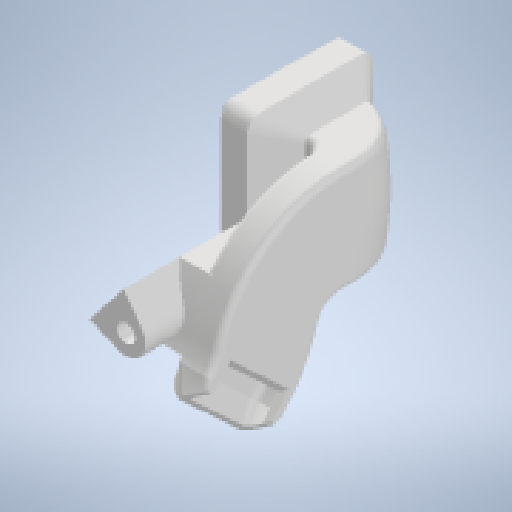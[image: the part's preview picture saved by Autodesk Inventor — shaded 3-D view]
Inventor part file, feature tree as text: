
AUTODESK INVENTOR PART (.ipt)
format: ipt  version: 2023 (Build 270158000, 158)  size: 883,712 bytes
history: native  units: in
note: dims shown in document units (in); Inventor stores cm internally (conversion verified against a paired STEP export)
features: sketch x22, extrude x15, plane x11, reference x9, other x8, loft x6, fillet x3, sweep x2, projected_geometry x2
ambient origin geometry x8: Origin, YZ Plane, XZ Plane, XY Plane, X Axis, Y Axis, Z Axis, Center Point
bodies: Solid1 (feature_tree)
feature tree (78):
  sketch  "Sketch1"  dims[d0=-0.1969in d1=0.7087in d2=0.0in]
  plane  "Work Plane1"
  extrude  "Extrusion1"  Depth=0.7087in TaperAngle=0.0deg
  plane  "Work Plane2"
  sketch  "Sketch3"  dims[d5=0.1575in d6=-0.1575in]
  plane  "Work Plane3"
  extrude  "Extrusion2"  Depth=0.2441in
  extrude  "Extrusion3"  [1 undecoded]
  plane  "Work Plane4"
  sketch  "Sketch5"  dims[d10=0.0984in d11=0.0in d12=-0.0787in]
  extrude  "Extrusion4"  Depth=0.0906in TaperAngle=0.0deg
  extrude  "Extrusion5"  [1 undecoded]
  extrude  "Extrusion6"  Depth=0.4961in
  fillet  "Fillet1"  Radius=0.7776in
  sketch  "Sketch7"  dims[d16=0.6122in d17=0.0394in]
  plane  "Work Plane5"
  sweep  "Sweep1"
  plane  "Work Plane7"
  sketch  "Sketch10"  dims[d20=0.0394in d21=0.0394in]
  loft  "Loft1"
  loft  "Loft2"
  extrude  "Extrusion8"  Depth=0.0689in
  extrude  "Extrusion9"  Depth=0.0689in
  plane  "Work Plane9"
  sketch  "Sketch15"  dims[d26=0.0689in d27=0.9843in]
  extrude  "Extrusion7"  Depth=0.9843in
  loft  "Loft3"
  loft  "Loft4"
  sketch  "Sketch18"  dims[d28=0.315in d29=0.1969in d30=0.0in]
  plane  "Work Plane12"
  sketch  "Sketch23"  dims[d31=0.0787in d32=0.0in d33=0.0787in]
  sketch  "Sketch24"  dims[d34=0.0787in d35=0.0in d36=0.1969in d37=0.0in]
  extrude  "Extrusion11"  Depth=0.1969in TaperAngle=0.0deg
  loft  "Loft6"
  loft  "Loft7"
  sweep  "Sweep2"
  fillet  "Fillet4"  Radius=0.0394in
  sketch  "Sketch30"  dims[d47=0.0in d49=0.125in]
  extrude  "Extrusion12"  Depth=0.0394in
  sketch  "Sketch28"  dims[d42=0.0394in d43=0.0394in d44=0.0394in]
  plane  "Work Plane16"
  extrude  "Extrusion13"  Depth=0.125in
  extrude  "Extrusion14"  Depth=0.5512in
  extrude  "Extrusion15"  TaperAngle=75.0deg  [1 undecoded]
  extrude  "Extrusion16"  Depth=0.1772in
  fillet  "Fillet5"  Radius=0.2756in
  reference  "Reference1"
  sketch  "Sketch2"  dims[d3=0.0906in d4=0.2441in]
  reference  "Reference2"
  reference  "Reference3"
  reference  "Reference4"
  reference  "Reference5"
  reference  "Reference6"
  sketch  "Sketch4"  dims[d7=0.2165in d8=0.0906in d9=0.0in]
  reference  "Reference7"
  sketch  "Sketch6"  dims[d13=0.689in d14=0.4961in d15=0.7776in]
  sketch  "Sketch8"  dims[d18=0.0394in d19=0.0394in]
  plane  "Work Plane6"
  other  "Edges1"
  other  "Edges2"
  sketch  "Sketch11"  dims[d22=0.0394in d23=0.0689in]
  sketch  "Sketch12"  dims[d24=0.0689in d25=0.0689in]
  other  "Edges3"
  projected_geometry  "Projected Loop2"
  plane  "Work Plane10"
  projected_geometry  "Projected Loop4"
  sketch  "3D Sketch1"
  sketch  "Sketch25"  dims[d38=0.0394in d39=0.5512in]
  sketch  "Sketch26"  dims[d40=0.1181in d41=0.2461in]
  reference  "Reference9"
  sketch  "Sketch29"  dims[d45=0.0394in d46=0.0394in]
  reference  "Reference10"
  sketch  "Sketch31"  dims[d50=0.0in d51=0.0in d52=0.5512in d53=75.0deg d54=0.1772in d56=0.2756in d57=0.7087in d58=30.0deg d71=0.0394in d72=0.0394in d73=0.0394in d74=0.0394in d75=0.0394in d76=0.0394in d77=0.0984in d78=0.5512in d79=0.0197in d80=0.0in d81=90.0deg d82=0.0in d83=90.0deg d84=0.0in d85=90.0deg d86=0.0in d87=90.0deg d90=0.3937in d91=0.0in d92=0.315in d93=0.0787in d94=0.0in d101=0.1181in d102=0.0394in d103=0.0394in d104=0.0394in d106=0.6299in d107=0.315in d108=0.0394in d109=0.0in d110=90.0deg d111=0.0in d112=90.0deg d113=0.0in d114=90.0deg d117=0.0in d118=90.0deg d121=0.2756in d122=90.0deg d123=0.0394in d124=0.0591in d132=90.0deg d133=90.0deg d134=0.0in d135=90.0deg d136=0.0in d137=90.0deg d138=0.0in d139=90.0deg d140=0.0in d141=90.0deg d143=0.0in d144=90.0deg d145=0.0in d146=90.0deg d147=0.0in d148=90.0deg d149=0.0in d150=90.0deg d151=0.0in d152=0.0in d153=0.1875in d154=0.0in d155=0.0276in d156=0.1063in d157=0.7087in d158=0.0in d159=0.1969in d160=0.0in d161=0.0394in d162=0.0in d163=0.7874in d164=0.0in d165=0.0394in d166=0.0in d167=0.3937in d168=0.0in d169=0.0787in]
  other  "<userpath>\Desktop\Another3dPrinterShroud\MODELS\ENDER 3 ASSEMBLY.iam"
  other  "ENDER 3 ASSEMBLY.iam"
  other  "FRONTPLATE:1"
  other  "<userpath> laptop\Desktop\Another3dPrinterShroud\MODELS\ENDER 3 ASSEMBLY.iam"
  other  "ENDER 3 NOZZLE:1"
note: 3 required parameter values undecoded (feature->parameter linkage not recoverable at this tier; creation-order binding heuristic only, values carry confidence <= 0.55)
